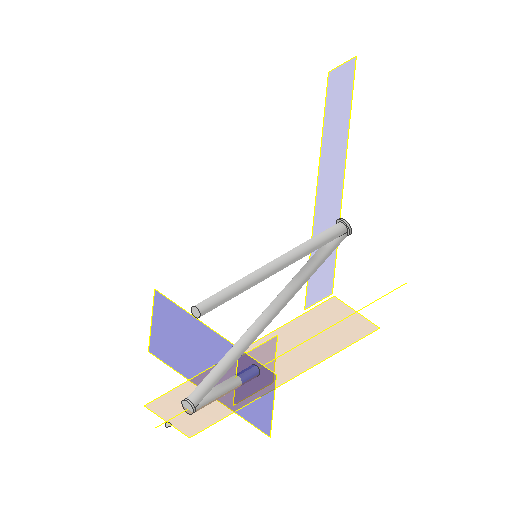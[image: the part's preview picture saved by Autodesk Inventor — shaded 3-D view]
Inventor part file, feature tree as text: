
AUTODESK INVENTOR PART (.ipt)
format: ipt  version: 2022 (Build 260153000, 153)  size: 166,400 bytes
history: native  units: mm
features: other x10, plane x8, sketch x5, projected_geometry x4, extrude x3, reference x2, sweep x1
ambient origin geometry x8: Origin, YZ Plane, XZ Plane, XY Plane, X Axis, Y Axis, Z Axis, Center Point
bodies: Solid1 (feature_tree)
feature tree (33):
  plane  "Work Plane1"
  plane  "Work Plane4"
  sketch  "Sketch1"  dims[d0=40.0mm d1=100.0mm]
  plane  "Work Plane7"
  sweep  "Sweep1"
  plane  "Work Plane8"
  extrude  "Extrusion1"  Depth=85.0mm
  extrude  "Extrusion2"  Depth=12.217305mm
  extrude  "Extrusion3"  TaperAngle=0.0deg  [1 undecoded]
  plane  "Arbeitsebene10"
  other  "Work Axis1"
  plane  "Work Plane2"
  other  "Work Point1"
  plane  "Work Plane3"
  sketch  "Sketch3"  dims[d2=30.0deg d3=85.0mm]
  reference  "Reference2"
  sketch  "Sketch4"  dims[d4=30.0deg d6=12.217305mm]
  projected_geometry  "Projected Loop1"
  projected_geometry  "Projected Loop2"
  projected_geometry  "Projected Loop3"
  reference  "Reference3"
  sketch  "Sketch5"  dims[d7=5.0mm d8=0.0mm d9=0.0mm]
  sketch  "Sketch6"  dims[d10=12.217305mm d11=7.0mm d12=7.0mm d13=10.0mm d14=0.0mm d15=1.0mm d16=0.0mm d17=1.0mm d18=0.0mm]
  projected_geometry  "Projected Loop4"
  other  "Arbeitsachse2"
  other  "Arbeitspunkt2"
  plane  "Arbeitsebene9"
  other  "cellSTORM_v5.iam"
  other  "10_Filteslide_25mm:1"
  other  "cellSTORM_Base_v0_R1:1"
  other  "<userpath>\Downloads\cellSTORM\cellSTORM_v5_microsocpe.iam"
  other  "cellSTORM_v5_microsocpe.iam"
  other  "cellSTORM_v5_opticalstage:1"
note: 1 required parameter value undecoded (feature->parameter linkage not recoverable at this tier; creation-order binding heuristic only, values carry confidence <= 0.55)
